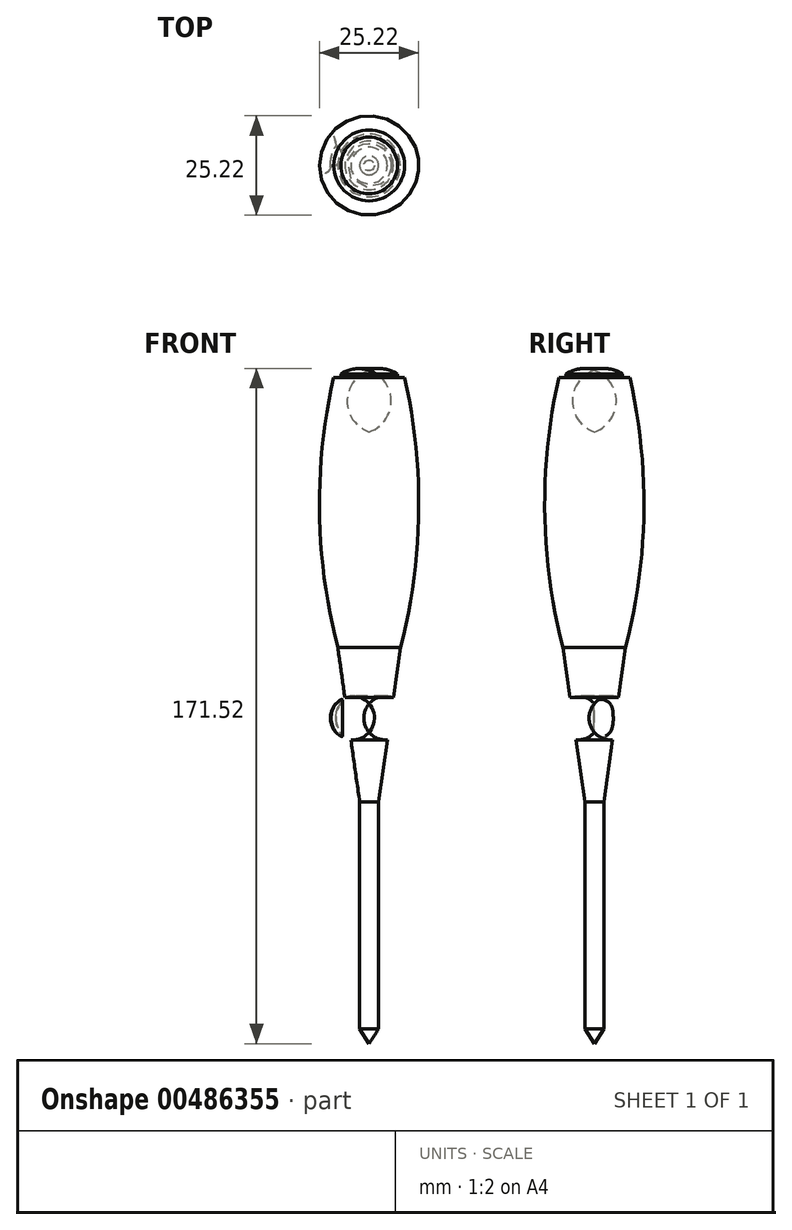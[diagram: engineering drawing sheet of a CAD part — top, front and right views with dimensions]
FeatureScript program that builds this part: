
annotation { "Feature Type Name" : "Feature", "Feature Type Description" : "" }
export const myFeature = defineFeature(function(context is Context, id is Id, definition is map)
    precondition{}
    {
        {
            var Q0;
            Q0=qCreatedBy(makeId("Front.planeOp"),FACE);
            var sketch = newSketch(context, id + "F0", { "sketchPlane" : qUnion([Q0])});
            skLineSegment(sketch, "E0", {"start": v(0, -55.2) * mm, "end": v(2.4, -51.45) * mm});
            skLineSegment(sketch, "E1", {"start": v(2.4, -51.45) * mm, "end": v(2.4, -14.2) * mm});
            skLineSegment(sketch, "E2", {"start": v(2.4, -14.2) * mm, "end": v(2.4, 6.2) * mm});
            skLineSegment(sketch, "E3", {"start": v(2.4, 6.2) * mm, "end": v(4.63, 21.97) * mm});
            skArc(sketch, "E4", {"start": v(7.95, 45.42) * mm, "mid": v(12.6, 79.7) * mm, "end": v(9, 114.1) * mm});
            skPoint(sketch, "E5.orphan", {"position": v(-1.13, 132.28) * mm});
            skPoint(sketch, "E6.start.orphan", {"position": v(0, 73.38) * mm});
            skLineSegment(sketch, "E7", {"start": v(0, -55.2) * mm, "end": v(0, 115.87) * mm});
            skPoint(sketch, "E8.center.orphan", {"position": v(-1.13, 119.36) * mm});
            skPoint(sketch, "E8.end.orphan", {"position": v(0, 124.8) * mm});
            skArc(sketch, "E9", {"start": v(7.2, 114.98) * mm, "mid": v(3.7, 116.25) * mm, "end": v(0, 115.87) * mm});
            skLineSegment(sketch, "E10", {"start": v(7.2, 114.98) * mm, "end": v(7.2, 114.1) * mm});
            skLineSegment(sketch, "E11", {"start": v(7.2, 114.1) * mm, "end": v(9, 114.1) * mm});
            skPoint(sketch, "E12.orphan", {"position": v(7.95, 118.43) * mm});
            skArc(sketch, "E13", {"start": v(4.63, 21.97) * mm, "mid": v(9.77, 26.76) * mm, "end": v(6.16, 32.78) * mm});
            skLineSegment(sketch, "E14.trimOffspring", {"start": v(6.16, 32.78) * mm, "end": v(7.95, 45.42) * mm});
            skSolve(sketch);
        }
        {
            var Q0;
            Q0 = qSketchRegion(id + "F0", true);
            var Q1;
            Q1=sQuery(id+"F0.wireOp",EDGE,"E7");
            revolve(context, id + "F1", {"entities" : qUnion([Q0]), "axis" : qUnion([Q1]), "revolveType" : RevolveType.FULL});
        }
        {
            var Q0;
            Q0=qCreatedBy(makeId("Top.planeOp"),FACE);
            var sketch = newSketch(context, id + "F2", { "sketchPlane" : qUnion([Q0])});
            skArc(sketch, "E15", {"start": v(-9.97, 0) * mm, "mid": v(-6.9, 1.83) * mm, "end": v(-8.71, 4.91) * mm});
            skArc(sketch, "E16.1.1", {"start": v(-4.98, -8.63) * mm, "mid": v(-5.03, -5.06) * mm, "end": v(-8.6, -5.09) * mm});
            skArc(sketch, "E16.2.1", {"start": v(4.98, -8.63) * mm, "mid": v(1.86, -6.89) * mm, "end": v(0.1, -10) * mm});
            skArc(sketch, "E16.3.1", {"start": v(9.97, 0) * mm, "mid": v(6.9, -1.83) * mm, "end": v(8.71, -4.91) * mm});
            skArc(sketch, "E16.4.1", {"start": v(4.98, 8.63) * mm, "mid": v(5.03, 5.06) * mm, "end": v(8.6, 5.09) * mm});
            skArc(sketch, "E16.5.1", {"start": v(-4.98, 8.63) * mm, "mid": v(-1.86, 6.89) * mm, "end": v(-0.1, 10) * mm});
            skPoint(sketch, "E16.center", {"position": v(0, 0) * mm});
            skArc(sketch, "E17", {"start": v(-8.71, 4.91) * mm, "mid": v(-10.33, 2.7) * mm, "end": v(-9.97, 0) * mm});
            skArc(sketch, "E18.1.0", {"start": v(-8.6, -5.09) * mm, "mid": v(-7.51, -7.6) * mm, "end": v(-4.98, -8.63) * mm});
            skArc(sketch, "E18.2.0", {"start": v(0.1, -10) * mm, "mid": v(2.82, -10.3) * mm, "end": v(4.98, -8.63) * mm});
            skArc(sketch, "E18.3.0", {"start": v(8.71, -4.91) * mm, "mid": v(10.33, -2.7) * mm, "end": v(9.97, 0) * mm});
            skArc(sketch, "E18.4.0", {"start": v(8.6, 5.09) * mm, "mid": v(7.51, 7.6) * mm, "end": v(4.98, 8.63) * mm});
            skArc(sketch, "E18.5.0", {"start": v(-0.1, 10) * mm, "mid": v(-2.82, 10.3) * mm, "end": v(-4.98, 8.63) * mm});
            skSolve(sketch);
        }
        {
            var Q0;
            Q0 = qSketchRegion(id + "F2", true);
            extrude(context, id + "F3", {"entities" : qUnion([Q0]), "operationType" : NewBodyOperationType.REMOVE, "depth" : 38.1 * mm, "offsetDistance" : 25.4 * mm});
        }
        {
            var Q0;
            Q0=makeQuery(id+"F3.boolean.opBoolean","INTERSECT",EDGE,{"derivedFrom":[makeQuery(id+"F1.opRevolve","SWEPT_FACE",FACE,{"disambiguationData":[OSD([sQuery(id+"F0.wireOp",EDGE,"E13")])]}),makeQuery(id+"F3.opExtrude","SWEPT_FACE",FACE,{"disambiguationData":[OSD([sQuery(id+"F2.wireOp",EDGE,"E16.1.1")])]})]});
            fillet(context, id + "F4", {"entities" : qUnion([Q0]), "radius" : 0.13 * mm, "tangentPropagation" : true, "allowEdgeOverflow" : false});
        }
        {
            var Q0;
            Q0=makeQuery(id+"F3.boolean.opBoolean","INTERSECT",EDGE,{"derivedFrom":[makeQuery(id+"F1.opRevolve","SWEPT_FACE",FACE,{"disambiguationData":[OSD([sQuery(id+"F0.wireOp",EDGE,"E13")])]}),makeQuery(id+"F3.opExtrude","SWEPT_FACE",FACE,{"disambiguationData":[OSD([sQuery(id+"F2.wireOp",EDGE,"E16.2.1")])]})]});
            var Q1;
            Q1=makeQuery(id+"F3.boolean.opBoolean","INTERSECT",EDGE,{"derivedFrom":[makeQuery(id+"F1.opRevolve","SWEPT_FACE",FACE,{"disambiguationData":[OSD([sQuery(id+"F0.wireOp",EDGE,"E13")])]}),makeQuery(id+"F3.opExtrude","SWEPT_FACE",FACE,{"disambiguationData":[OSD([sQuery(id+"F2.wireOp",EDGE,"E16.3.1")])]})]});
            var Q2;
            Q2=makeQuery(id+"F3.boolean.opBoolean","INTERSECT",EDGE,{"derivedFrom":[makeQuery(id+"F1.opRevolve","SWEPT_FACE",FACE,{"disambiguationData":[OSD([sQuery(id+"F0.wireOp",EDGE,"E13")])]}),makeQuery(id+"F3.opExtrude","SWEPT_FACE",FACE,{"disambiguationData":[OSD([sQuery(id+"F2.wireOp",EDGE,"E16.4.1")])]})]});
            var Q3;
            Q3=makeQuery(id+"F3.boolean.opBoolean","INTERSECT",EDGE,{"derivedFrom":[makeQuery(id+"F1.opRevolve","SWEPT_FACE",FACE,{"disambiguationData":[OSD([sQuery(id+"F0.wireOp",EDGE,"E13")])]}),makeQuery(id+"F3.opExtrude","SWEPT_FACE",FACE,{"disambiguationData":[OSD([sQuery(id+"F2.wireOp",EDGE,"E16.5.1")])]})]});
            var Q4;
            Q4=makeQuery(id+"F3.boolean.opBoolean","INTERSECT",EDGE,{"derivedFrom":[makeQuery(id+"F1.opRevolve","SWEPT_FACE",FACE,{"disambiguationData":[OSD([sQuery(id+"F0.wireOp",EDGE,"E13")])]}),makeQuery(id+"F3.opExtrude","SWEPT_FACE",FACE,{"disambiguationData":[OSD([sQuery(id+"F2.wireOp",EDGE,"E15")])]})]});
            fillet(context, id + "F5", {"entities" : qUnion([Q0, Q1, Q2, Q3, Q4]), "radius" : 0.13 * mm, "tangentPropagation" : true, "allowEdgeOverflow" : false});
        }
    });
